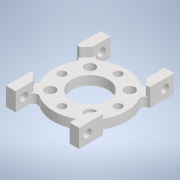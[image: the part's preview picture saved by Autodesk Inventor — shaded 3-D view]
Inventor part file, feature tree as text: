
AUTODESK INVENTOR PART (.ipt)
format: ipt  version: 2020.1 (Build 241239000, 239)  size: 173,056 bytes
history: native  units: in
note: dims shown in document units (in); Inventor stores cm internally (conversion verified against a paired STEP export)
features: mirror x1
ambient origin geometry x8: Origin, YZ Plane, XZ Plane, XY Plane, X Axis, Y Axis, Z Axis, Center Point
bodies: Solid1 (feature_tree)
feature tree (1):
  mirror  "Mirror6"
